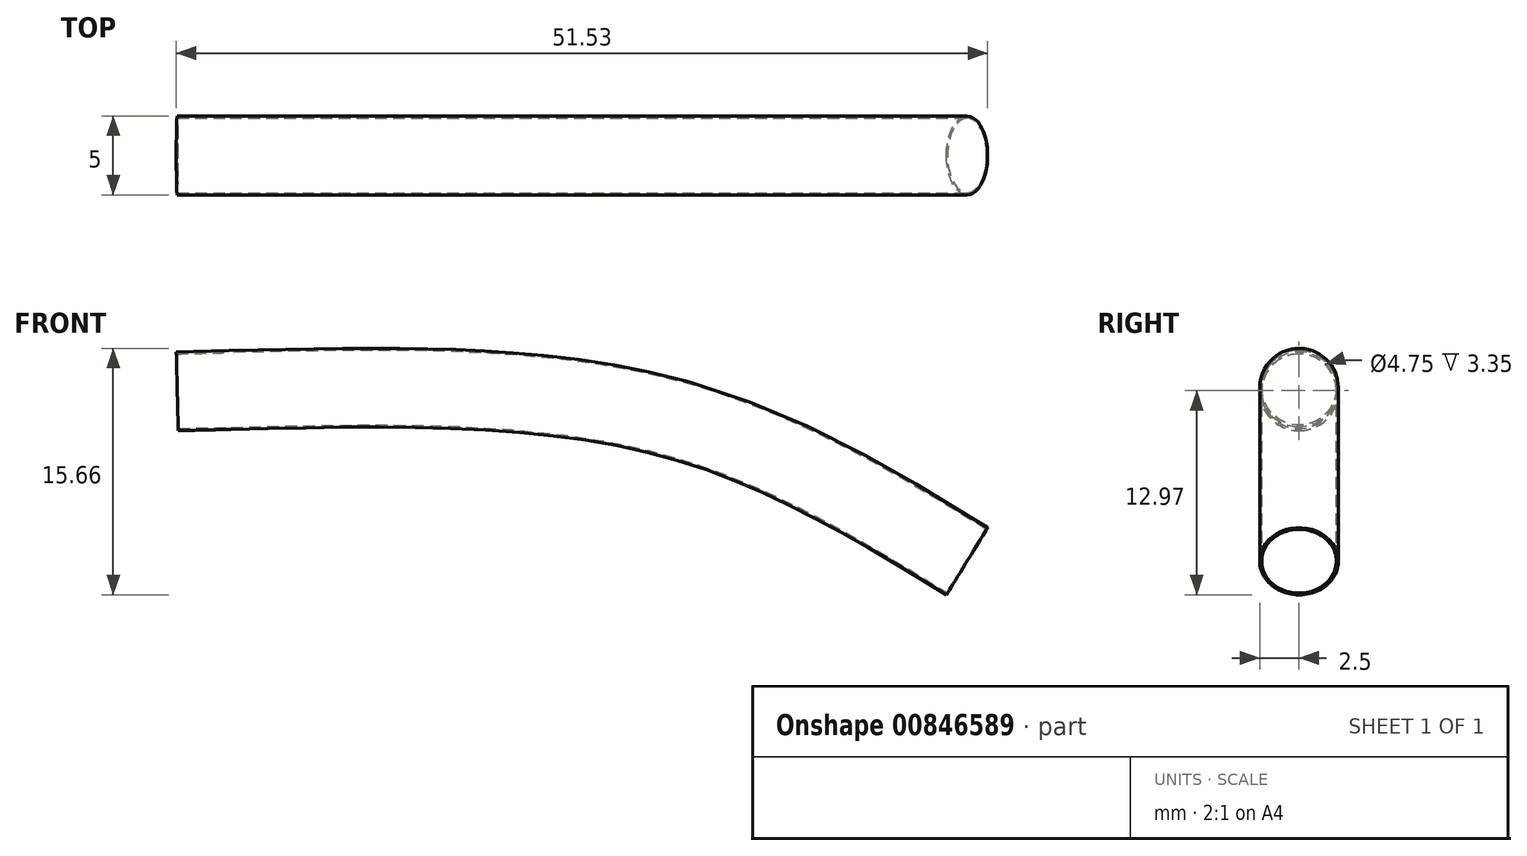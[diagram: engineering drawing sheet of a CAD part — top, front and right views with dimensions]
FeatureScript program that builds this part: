
annotation { "Feature Type Name" : "Feature", "Feature Type Description" : "" }
export const myFeature = defineFeature(function(context is Context, id is Id, definition is map)
    precondition{}
    {
        {
            var Q0;
            Q0=qCreatedBy(makeId("Front.planeOp"),FACE);
            var sketch = newSketch(context, id + "F0", { "sketchPlane" : qUnion([Q0])});
            skFitSpline(sketch, "E0", {"points": [v(-33.25, 0) * mm, v(-5.62, -1.66) * mm, v(13.54, -10.87) * mm], "startDerivative": vector(54.73, 1.32) * mm, "endDerivative": vector(38.5, -23.6) * mm});
            skSolve(sketch);
        }
        {
            var Q0;
            Q0=sQuery(id+"F0.wireOp",EDGE,"E0");
            var Q1;
            Q1=sQuery(id+"F0.wireOp",VERTEX,"E0.end");
            cPlane(context, id + "F1", {"entities" : qUnion([Q0, Q1]), "cplaneType" : CPlaneType.CURVE_POINT, "offset" : 25 * mm, "width" : 150 * mm, "height" : 150 * mm});
        }
        {
            var Q0;
            Q0=qCreatedBy(id+"F1.planeOp",FACE);
            var sketch = newSketch(context, id + "F2", { "sketchPlane" : qUnion([Q0])});
            skCircle(sketch, "E1", {"center": v(0, -2.14) * mm, "radius": 2.5 * mm});
            skSolve(sketch);
        }
        {
            var Q0;
            Q0=makeQuery(id+"F2.imprint","IMPRINT",FACE,{"disambiguationData":[TD([[makeQuery(id+"F2.imprint","IMPRINT",EDGE,{"derivedFrom":sQuery(id+"F2.wireOp",EDGE,"E1")}),1.0]])]});
            var Q1;
            Q1=sQuery(id+"F0.wireOp",EDGE,"E0");
            sweep(context, id + "F3", {"profiles" : qUnion([Q0]), "path" : qUnion([Q1])});
        }
        {
            var Q0;
            Q0=makeQuery(id+"F3.opSweep","CAP_FACE",FACE,{"disambiguationData":[OSD([sQuery(id+"F0.wireOp",VERTEX,"E0.start"),sQuery(id+"F2.wireOp",EDGE,"E1")])],"isStart":false});
            var Q1;
            Q1=makeQuery(id+"F3.opSweep","CAP_FACE",FACE,{"disambiguationData":[OSD([sQuery(id+"F0.wireOp",VERTEX,"E0.end"),sQuery(id+"F2.wireOp",EDGE,"E1")])],"isStart":true});
            shell(context, id + "F4", {"entities" : qUnion([Q0, Q1]), "thickness" : .125 * mm});
        }
        {
            var Q0;
            Q0=makeQuery(id+"F3.opSweep","CAP_FACE",FACE,{"disambiguationData":[OSD([sQuery(id+"F0.wireOp",VERTEX,"E0.start"),sQuery(id+"F2.wireOp",EDGE,"E1")])],"isStart":false});
            extrude(context, id + "F5", {"entities" : qUnion([Q0]), "operationType" : NewBodyOperationType.ADD, "depth" : 3.35 * mm, "offsetDistance" : 25 * mm});
        }
    });
